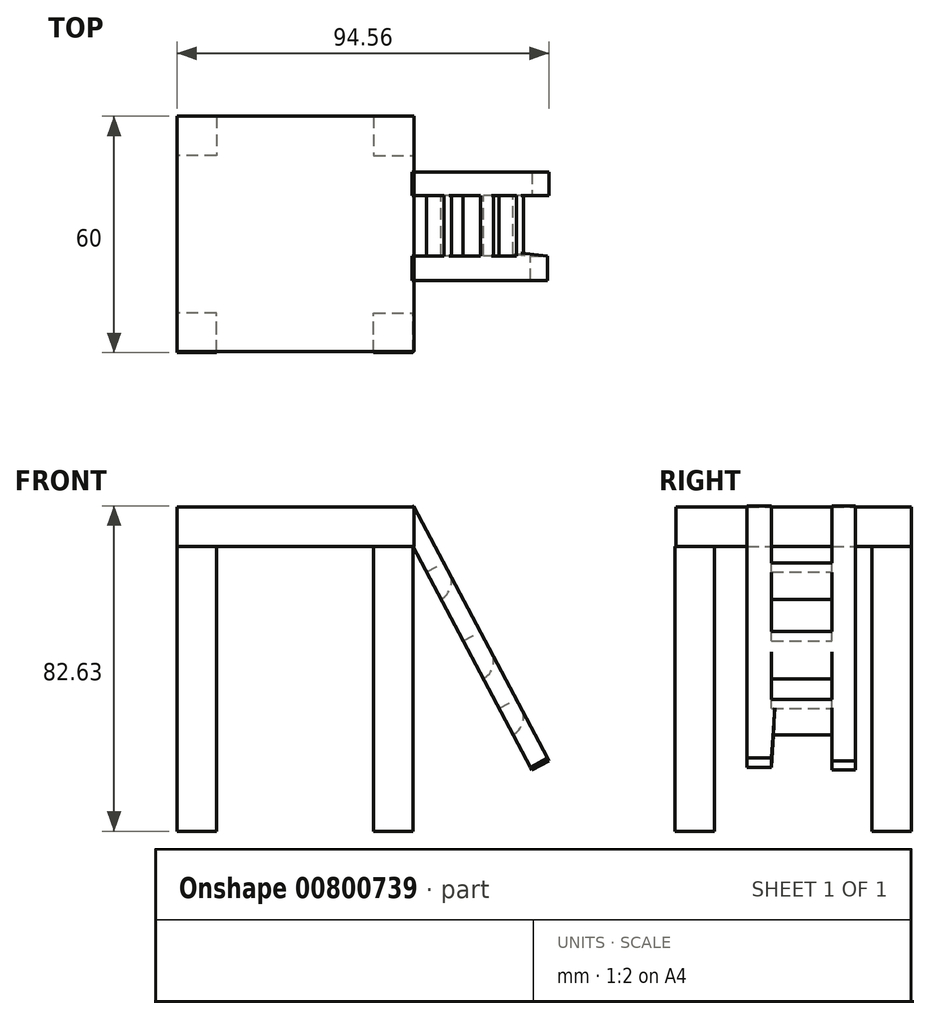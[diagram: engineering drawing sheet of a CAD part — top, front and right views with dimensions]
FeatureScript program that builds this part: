
annotation { "Feature Type Name" : "Feature", "Feature Type Description" : "" }
export const myFeature = defineFeature(function(context is Context, id is Id, definition is map)
    precondition{}
    {
        {
            var Q0;
            Q0=qCreatedBy(makeId("Top.planeOp"),FACE);
            var sketch = newSketch(context, id + "F0", { "sketchPlane" : qUnion([Q0])});
            skLineSegment(sketch, "E0.bottom", {"start": v(20, 30) * mm, "end": v(30, 30) * mm});
            skLineSegment(sketch, "E0.top", {"start": v(20, 20) * mm, "end": v(30, 20) * mm});
            skLineSegment(sketch, "E0.left", {"start": v(20, 30) * mm, "end": v(20, 20) * mm});
            skLineSegment(sketch, "E0.right", {"start": v(30, 30) * mm, "end": v(30, 20) * mm});
            skLineSegment(sketch, "E1", {"start": v(0, -27.59) * mm, "end": v(0, 60.52) * mm, "construction": true});
            skLineSegment(sketch, "E2.MirrorCS", {"start": v(-20, 30) * mm, "end": v(-30, 30) * mm});
            skLineSegment(sketch, "E3.MirrorCS", {"start": v(-20, 30) * mm, "end": v(-20, 20) * mm});
            skLineSegment(sketch, "E4.MirrorCS", {"start": v(-20, 20) * mm, "end": v(-30, 20) * mm});
            skLineSegment(sketch, "E5.MirrorCS", {"start": v(-30, 30) * mm, "end": v(-30, 20) * mm});
            skLineSegment(sketch, "E6", {"start": v(-40.94, 0) * mm, "end": v(43.04, 0) * mm, "construction": true});
            skLineSegment(sketch, "E7.MirrorCS", {"start": v(20, -30) * mm, "end": v(30, -30) * mm});
            skLineSegment(sketch, "E8.MirrorCS", {"start": v(-30, -30) * mm, "end": v(-30, -20) * mm});
            skLineSegment(sketch, "E9.MirrorCS", {"start": v(20, -20) * mm, "end": v(30, -20) * mm});
            skLineSegment(sketch, "E10.MirrorCS", {"start": v(-20, -20) * mm, "end": v(-30, -20) * mm});
            skLineSegment(sketch, "E11.MirrorCS", {"start": v(-20, -30) * mm, "end": v(-30, -30) * mm});
            skLineSegment(sketch, "E12.MirrorCS", {"start": v(0, 27.59) * mm, "end": v(0, -60.52) * mm, "construction": true});
            skLineSegment(sketch, "E13.MirrorCS", {"start": v(-20, -30) * mm, "end": v(-20, -20) * mm});
            skLineSegment(sketch, "E14.MirrorCS", {"start": v(30, -30) * mm, "end": v(30, -20) * mm});
            skLineSegment(sketch, "E15.MirrorCS", {"start": v(20, -30) * mm, "end": v(20, -20) * mm});
            skSolve(sketch);
        }
        {
            var Q0;
            Q0 = qSketchRegion(id + "F0", true);
            extrude(context, id + "F1", {"entities" : qUnion([Q0]), "depth" : 72.4 * mm, "offsetDistance" : 25 * mm});
        }
        {
            var Q0;
            Q0=makeQuery(id+"F1.opExtrude","CAP_FACE",FACE,{"disambiguationData":[OSD([sQuery(id+"F0.wireOp",EDGE,"E2.MirrorCS"),sQuery(id+"F0.wireOp",EDGE,"E3.MirrorCS"),sQuery(id+"F0.wireOp",EDGE,"E4.MirrorCS"),sQuery(id+"F0.wireOp",EDGE,"E5.MirrorCS")])],"isStart":false});
            var sketch = newSketch(context, id + "F2", { "sketchPlane" : qUnion([Q0])});
            skLineSegment(sketch, "E16.bottom", {"start": v(-30, 30) * mm, "end": v(30.29, 30) * mm});
            skLineSegment(sketch, "E16.top", {"start": v(-30, -29.8) * mm, "end": v(30.29, -29.8) * mm});
            skLineSegment(sketch, "E16.left", {"start": v(-30, 30) * mm, "end": v(-30, -29.8) * mm});
            skLineSegment(sketch, "E16.right", {"start": v(30.29, 30) * mm, "end": v(30.29, -29.8) * mm});
            skSolve(sketch);
        }
        {
            var Q0;
            Q0 = qSketchRegion(id + "F2", true);
            extrude(context, id + "F3", {"entities" : qUnion([Q0]), "depth" : 10 * mm, "offsetDistance" : 25 * mm});
        }
        {
            var Q0;
            Q0=makeQuery(id+"F3.opExtrude","SWEPT_FACE",FACE,{"disambiguationData":[OSD([sQuery(id+"F2.wireOp",EDGE,"E16.right")])]});
            var Q1;
            Q1=makeQuery(id+"F3.opExtrude","CAP_EDGE",EDGE,{"disambiguationData":[OSD([sQuery(id+"F2.wireOp",EDGE,"E16.right")])],"isStart":false});
            cPlane(context, id + "F4", {"entities" : qUnion([Q0, Q1]), "cplaneType" : CPlaneType.LINE_ANGLE, "offset" : 25 * mm, "angle" : 152 * degree, "oppositeDirection" : true, "width" : 150 * mm, "height" : 150 * mm});
        }
        {
            var Q0;
            Q0=qCreatedBy(id+"F4.planeOp",FACE);
            var sketch = newSketch(context, id + "F5", { "sketchPlane" : qUnion([Q0])});
            skLineSegment(sketch, "E17", {"start": v(-11.72, 58.8) * mm, "end": v(-11.72, -13.7) * mm});
            skLineSegment(sketch, "E18", {"start": v(-11.72, -13.7) * mm, "end": v(-5.49, -13.7) * mm});
            skLineSegment(sketch, "E19", {"start": v(-5.49, 3.19) * mm, "end": v(-5.49, 11.77) * mm});
            skLineSegment(sketch, "E20", {"start": v(-11.72, 58.8) * mm, "end": v(-5.49, 58.8) * mm});
            skLineSegment(sketch, "E21", {"start": v(15.82, 58.8) * mm, "end": v(15.82, -14.48) * mm});
            skLineSegment(sketch, "E22", {"start": v(15.82, -14.48) * mm, "end": v(9.85, -14.48) * mm});
            skLineSegment(sketch, "E23", {"start": v(9.85, -14.48) * mm, "end": v(9.85, -4.35) * mm});
            skLineSegment(sketch, "E24", {"start": v(-5.49, 42.43) * mm, "end": v(9.85, 42.43) * mm});
            skLineSegment(sketch, "E25", {"start": v(-5.49, 34.64) * mm, "end": v(9.85, 34.64) * mm});
            skLineSegment(sketch, "E26", {"start": v(-5.49, 22.68) * mm, "end": v(9.85, 22.68) * mm});
            skLineSegment(sketch, "E27", {"start": v(-5.49, 11.77) * mm, "end": v(9.85, 11.77) * mm});
            skLineSegment(sketch, "E28", {"start": v(-5.49, 3.19) * mm, "end": v(9.85, 3.19) * mm});
            skLineSegment(sketch, "E29", {"start": v(-4.97, -4.35) * mm, "end": v(9.85, -4.35) * mm});
            skLineSegment(sketch, "E30.trimOffspring", {"start": v(9.85, 58.8) * mm, "end": v(15.82, 58.8) * mm});
            skLineSegment(sketch, "E31.trimOffspring", {"start": v(9.85, 42.43) * mm, "end": v(9.85, 58.8) * mm});
            skLineSegment(sketch, "E32.trimOffspring", {"start": v(-5.49, 42.43) * mm, "end": v(-5.49, 59.07) * mm});
            skLineSegment(sketch, "E33.trimOffspring", {"start": v(9.85, 22.68) * mm, "end": v(9.85, 34.64) * mm});
            skLineSegment(sketch, "E34.trimOffspring", {"start": v(-5.49, 22.68) * mm, "end": v(-5.49, 34.64) * mm});
            skLineSegment(sketch, "E35.trimOffspring", {"start": v(9.85, 3.19) * mm, "end": v(9.85, 11.77) * mm});
            skLineSegment(sketch, "E36", {"start": v(-4.97, -4.35) * mm, "end": v(-5.49, -13.7) * mm});
            skSolve(sketch);
        }
        {
            var Q0;
            Q0 = qSketchRegion(id + "F5", true);
            extrude(context, id + "F6", {"entities" : qUnion([Q0]), "operationType" : NewBodyOperationType.ADD, "oppositeDirection" : true, "depth" : 5 * mm, "offsetDistance" : 25 * mm});
        }
        {
            var Q0;
            Q0=makeQuery(id+"F6.opExtrude","CAP_EDGE",EDGE,{"disambiguationData":[OSD([sQuery(id+"F5.wireOp",EDGE,"E25")])],"isStart":true});
            var Q1;
            Q1=makeQuery(id+"F6.opExtrude","CAP_EDGE",EDGE,{"disambiguationData":[OSD([sQuery(id+"F5.wireOp",EDGE,"E27")])],"isStart":true});
            var Q2;
            Q2=makeQuery(id+"F6.opExtrude","CAP_EDGE",EDGE,{"disambiguationData":[OSD([sQuery(id+"F5.wireOp",EDGE,"E29")])],"isStart":true});
            fillet(context, id + "F7", {"entities" : qUnion([Q0, Q1, Q2]), "radius" : 5 * mm, "tangentPropagation" : true, "allowEdgeOverflow" : false});
        }
    });
